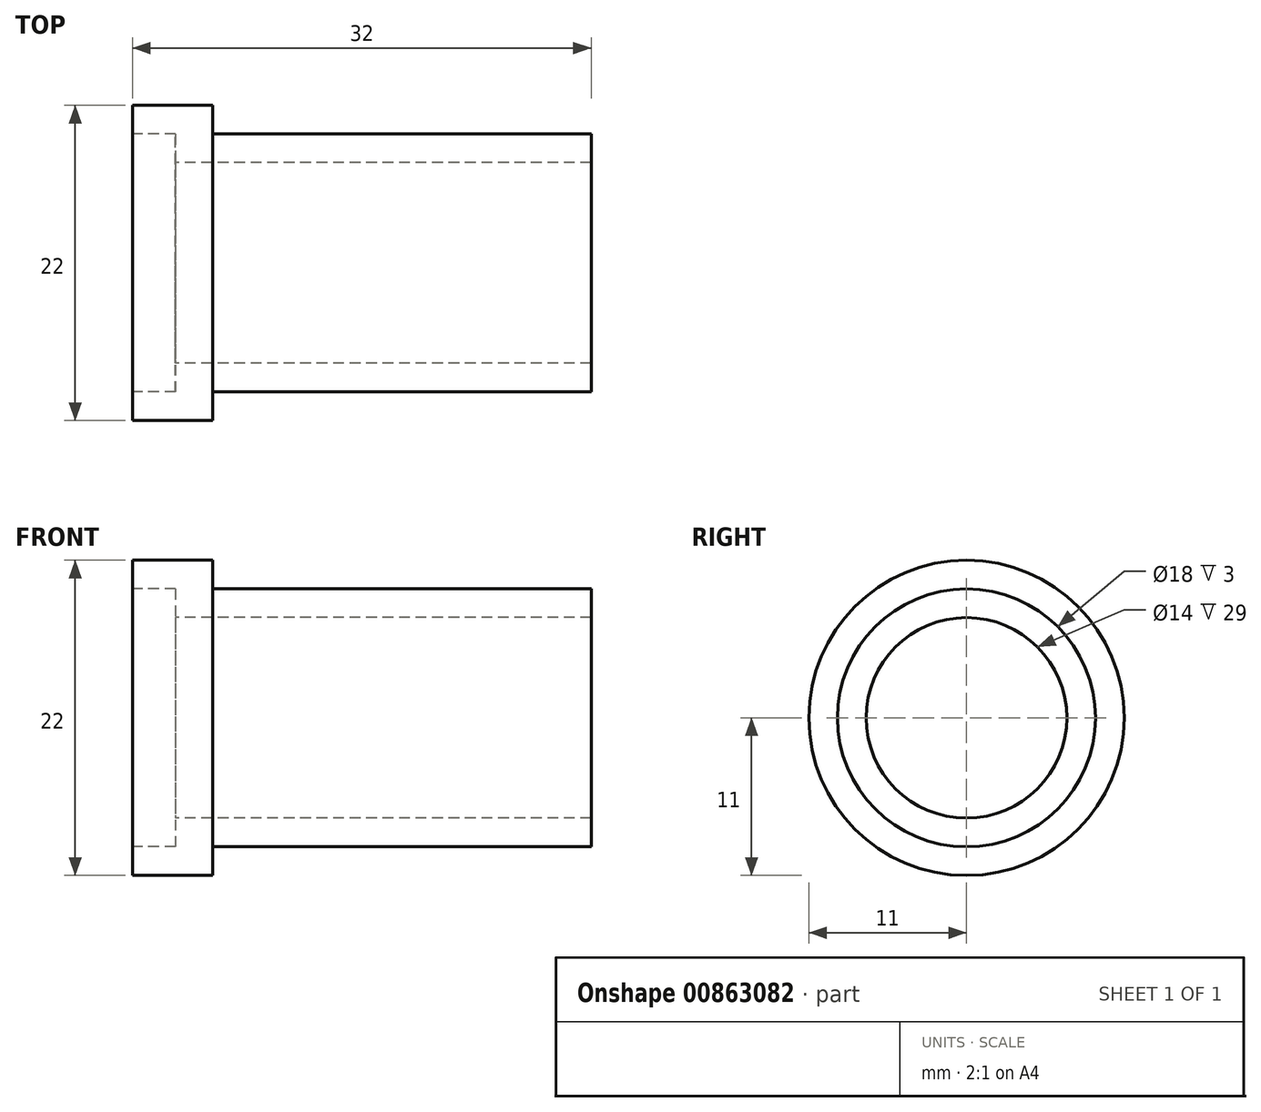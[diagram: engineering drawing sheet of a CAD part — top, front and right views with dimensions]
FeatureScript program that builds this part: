
annotation { "Feature Type Name" : "Feature", "Feature Type Description" : "" }
export const myFeature = defineFeature(function(context is Context, id is Id, definition is map)
    precondition{}
    {
        {
            var Q0;
            Q0=qCreatedBy(makeId("Front.planeOp"),FACE);
            var sketch = newSketch(context, id + "F0", { "sketchPlane" : qUnion([Q0])});
            skLineSegment(sketch, "E0", {"start": v(0, 9) * mm, "end": v(0, 11) * mm});
            skLineSegment(sketch, "E1", {"start": v(0, 11) * mm, "end": v(5.6, 11) * mm});
            skLineSegment(sketch, "E2", {"start": v(5.6, 11) * mm, "end": v(5.6, 9) * mm});
            skLineSegment(sketch, "E3", {"start": v(5.6, 9) * mm, "end": v(32, 9) * mm});
            skLineSegment(sketch, "E4", {"start": v(32, 9) * mm, "end": v(32, 7) * mm});
            skLineSegment(sketch, "E5", {"start": v(32, 7) * mm, "end": v(3, 7) * mm});
            skLineSegment(sketch, "E6", {"start": v(3, 7) * mm, "end": v(3, 9) * mm});
            skLineSegment(sketch, "E7", {"start": v(3, 9) * mm, "end": v(0, 9) * mm});
            skLineSegment(sketch, "E8", {"start": v(0, 0) * mm, "end": v(32, 0) * mm, "construction": true});
            skPoint(sketch, "E8.endSnap0", {"position": v(32, 8) * mm});
            skSolve(sketch);
        }
        {
            var Q0;
            Q0=makeQuery(id+"F0.imprint","IMPRINT",FACE,{"disambiguationData":[TD([[makeQuery(id+"F0.imprint","IMPRINT",EDGE,{"derivedFrom":sQuery(id+"F0.wireOp",EDGE,"E0")}),-1.0]])]});
            var Q1;
            Q1=sQuery(id+"F0.wireOp",EDGE,"E8");
            revolve(context, id + "F1", {"surfaceOperationType" : NewSurfaceOperationType.NEW, "entities" : qUnion([Q0]), "axis" : qUnion([Q1]), "revolveType" : RevolveType.FULL});
        }
    });
